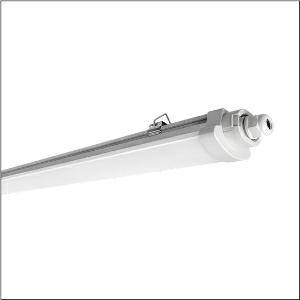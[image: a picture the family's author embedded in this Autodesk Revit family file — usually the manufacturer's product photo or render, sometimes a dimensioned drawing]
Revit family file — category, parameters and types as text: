
# Revit family: monsun_r__41_51fk20mn460a_a5b0
name_source: partatom
category: Lighting Fixtures
units: mm (PartAtom-declared; Revit-internal decimal feet)

## family parameters
Cut with Voids When Loaded = No
Host = Face
Light Source = No
Part Type = Normal
Room Calculation Point = No
Round Connector Dimension = Use Diameter
Shared = No

## types (1)
- --- (1 x LED, 6000 lm, 46 W, 4000K)
    Apparent Load = 46 VA
    CIE Flux Codes = 44 74 91 91 100
    Color Rendering = 80
    Color Temperature = 4000K
    Default Elevation = 1800 mm
    Description = Monsun® 41, damp-proof luminaire, primary optical cover: diffuser, of PC, frosted, light emission: direct distribution, primary light characteristic: symmetric, installation type: suspended mounting, surface-mounted, LED, rated luminous flux: 6.000lm, luminous efficacy: 130lm/W, light colour: 840, colour temperature: 4000K, control gear: ECG Multilumen, with terminal, 3-pole, mains connection: 220..240V, AC, 50/60Hz, rated input power: 46W, housing, luminaire housing, of PC, grey, length: 1.500mm, width: 79mm, height: 52mm, end cap, of PC, grey, ceiling mounting element, of stainless steel (V2A), protection rating (complete): IP65, insulation class (complete): insulation class II (safety insulation), certification: CE, UKCA, protection symbol: D, impact resistance: IK08, permissible operating ambient temperature: -20..+35°C, corresponds to IFS (International Featured Standards) requirements for safety and quality in the food industry, contact your sales advisor before using the luminaires in applications with unclear chemical exposure, large temperature fluctuations or condensation-forming humidity, packaging unit: 1 piece
    Height = 54 mm
    Lamp = 1 x LED
    Lamp Light Flux = 6000 lm
    Lamp Power = 46 W
    Lamp count = 1
    Length = 1500 mm
    Luminous efficacy = 130 lm/W
    Manufacturer = Siteco
    ModVariant = No
    Model = 51FK20MN460A
    Mounting Place = Ceiling
    Mounting Type = Surface mounted
    Number of Poles = 1
    OnlyDefault = Yes
    Power Factor = 1
    Product Name = Monsun® 41
    Product group = damp-proof luminaire
    ProductGroupID = 301
    Protection Class = Protection class II
    Protection Degree = IP 65
    RLX_Detail_Level = 1
    RLX_Emergency_Light_Flux = 0 lm
    RLX_Emergency_Type = 0
    RLX_Emergency_Type_DB = No
    RlxData = <blob elided: 28869 chars, md5=22aeccdd>
    Socket = socket
    Standby Power = 0 W
    System Light Flux = 6000 lm
    System Power = 46 W
    Type Comments = factory setting: luminous flux: 100 % | (HIGH)
    Type Image = l_1007037.jpg
    URL = http://relux.com
    VarID = @adj_125701
    Voltage = 0 V
    Weight = 0.00 kg
    Width = 79 mm

## geometry (parser evidence)
native form markers: Blend x4, Sweep x15
no freeform markers — native parametric forms only
